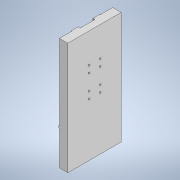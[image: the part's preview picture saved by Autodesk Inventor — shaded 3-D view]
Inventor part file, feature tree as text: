
AUTODESK INVENTOR PART (.ipt)
format: ipt  version: 2020.1 (Build 241239000, 239)  size: 158,720 bytes
history: native  units: mm
features: extrude x4, sketch x4, projected_geometry x3, other x1
ambient origin geometry x8: Origin, YZ Plane, XZ Plane, XY Plane, X Axis, Y Axis, Z Axis, Center Point
bodies: Body1 (feature_tree)
feature tree (12):
  other  "Твердое тело1"
  extrude  "Выдавливание1"  Depth=190.0mm
  extrude  "Выдавливание2"  Depth=30.0mm
  extrude  "Выдавливание3"  Depth=32.0mm
  extrude  "Выдавливание4"  Depth=44.0mm
  sketch  "Эскиз1"
  sketch  "Эскиз2"
  projected_geometry  "Спроецированная петля1"
  sketch  "Эскиз3"
  projected_geometry  "Спроецированная петля2"
  projected_geometry  "Спроецированная петля3"
  sketch  "Эскиз4"
